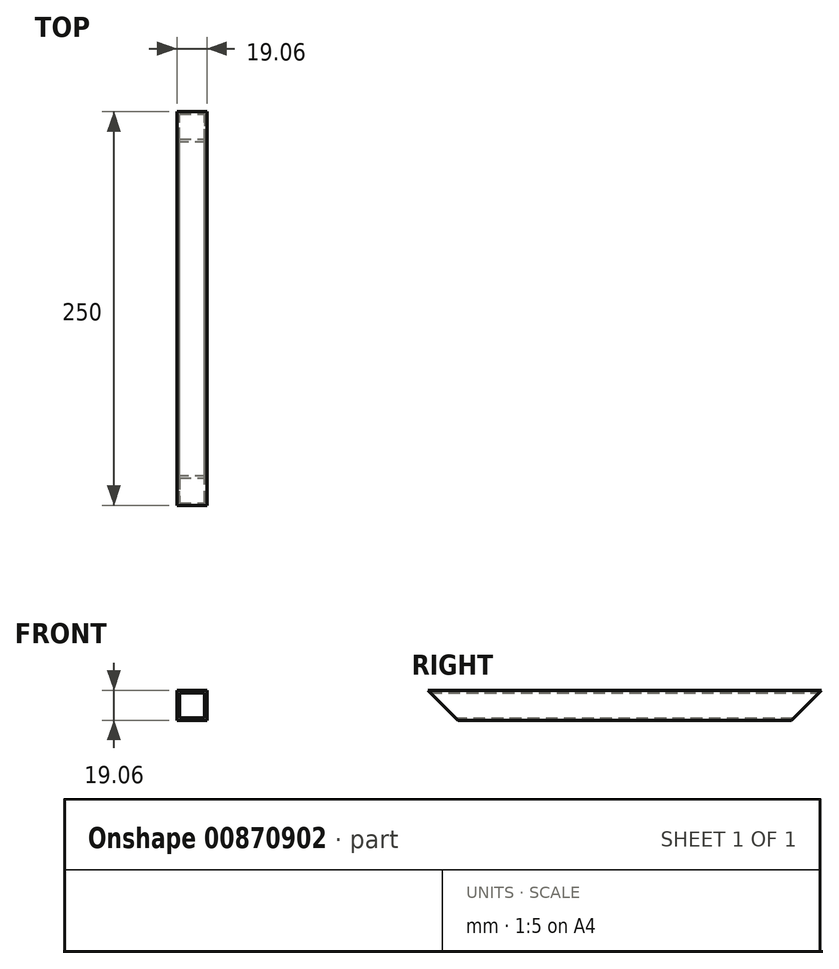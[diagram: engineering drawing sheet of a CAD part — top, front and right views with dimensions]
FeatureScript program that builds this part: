
annotation { "Feature Type Name" : "Feature", "Feature Type Description" : "" }
export const myFeature = defineFeature(function(context is Context, id is Id, definition is map)
    precondition{}
    {
        {
            var Q0;
            Q0=qCreatedBy(makeId("Front.planeOp"),FACE);
            var sketch = newSketch(context, id + "F0", { "sketchPlane" : qUnion([Q0])});
            skLineSegment(sketch, "E0.bottom", {"start": v(9.53, 9.53) * mm, "end": v(-9.53, 9.53) * mm});
            skLineSegment(sketch, "E0.top", {"start": v(9.53, -9.53) * mm, "end": v(-9.53, -9.53) * mm});
            skLineSegment(sketch, "E0.left", {"start": v(9.53, 9.53) * mm, "end": v(9.53, -9.53) * mm});
            skLineSegment(sketch, "E0.right", {"start": v(-9.53, 9.53) * mm, "end": v(-9.53, -9.53) * mm});
            skPoint(sketch, "E0.middle", {"position": v(0, 0) * mm});
            skLineSegment(sketch, "E1.bottom", {"start": v(7.94, 7.94) * mm, "end": v(-7.94, 7.94) * mm});
            skLineSegment(sketch, "E1.top", {"start": v(7.94, -7.94) * mm, "end": v(-7.94, -7.94) * mm});
            skLineSegment(sketch, "E1.left", {"start": v(7.94, 7.94) * mm, "end": v(7.94, -7.94) * mm});
            skLineSegment(sketch, "E1.right", {"start": v(-7.94, 7.94) * mm, "end": v(-7.94, -7.94) * mm});
            skSolve(sketch);
        }
        {
            var Q0;
            Q0 = qSketchRegion(id + "F0", true);
            extrude(context, id + "F1", {"entities" : qUnion([Q0]), "depth" : 250 * mm, "offsetDistance" : 25 * mm});
        }
        {
            var Q0;
            Q0=qCreatedBy(makeId("Right.planeOp"),FACE);
            var sketch = newSketch(context, id + "F2", { "sketchPlane" : qUnion([Q0])});
            skPoint(sketch, "E2", {"position": v(0, 0) * mm});
            skLineSegment(sketch, "E3", {"start": v(0, 9.53) * mm, "end": v(0, -9.53) * mm});
            skLineSegment(sketch, "E4", {"start": v(0, -9.53) * mm, "end": v(-19.05, -9.53) * mm});
            skLineSegment(sketch, "E5", {"start": v(-19.05, -9.53) * mm, "end": v(0, 9.53) * mm});
            skPoint(sketch, "E6", {"position": v(-250, 0) * mm});
            skLineSegment(sketch, "E7", {"start": v(-250, -9.52) * mm, "end": v(-250, 9.53) * mm});
            skLineSegment(sketch, "E8", {"start": v(-250, -9.53) * mm, "end": v(-230.95, -9.53) * mm});
            skLineSegment(sketch, "E9", {"start": v(-230.95, -9.52) * mm, "end": v(-250, 9.53) * mm});
            skSolve(sketch);
        }
        {
            var Q0;
            Q0 = qSketchRegion(id + "F2", true);
            extrude(context, id + "F3", {"entities" : qUnion([Q0]), "operationType" : NewBodyOperationType.REMOVE, "endBound" : BoundingType.THROUGH_ALL, "oppositeDirection" : true, "depth" : 25 * mm, "offsetDistance" : 25 * mm});
        }
        {
            var Q0;
            Q0 = qSketchRegion(id + "F2", true);
            extrude(context, id + "F4", {"entities" : qUnion([Q0]), "operationType" : NewBodyOperationType.REMOVE, "endBound" : BoundingType.THROUGH_ALL, "depth" : 25 * mm, "offsetDistance" : 25 * mm});
        }
    });
